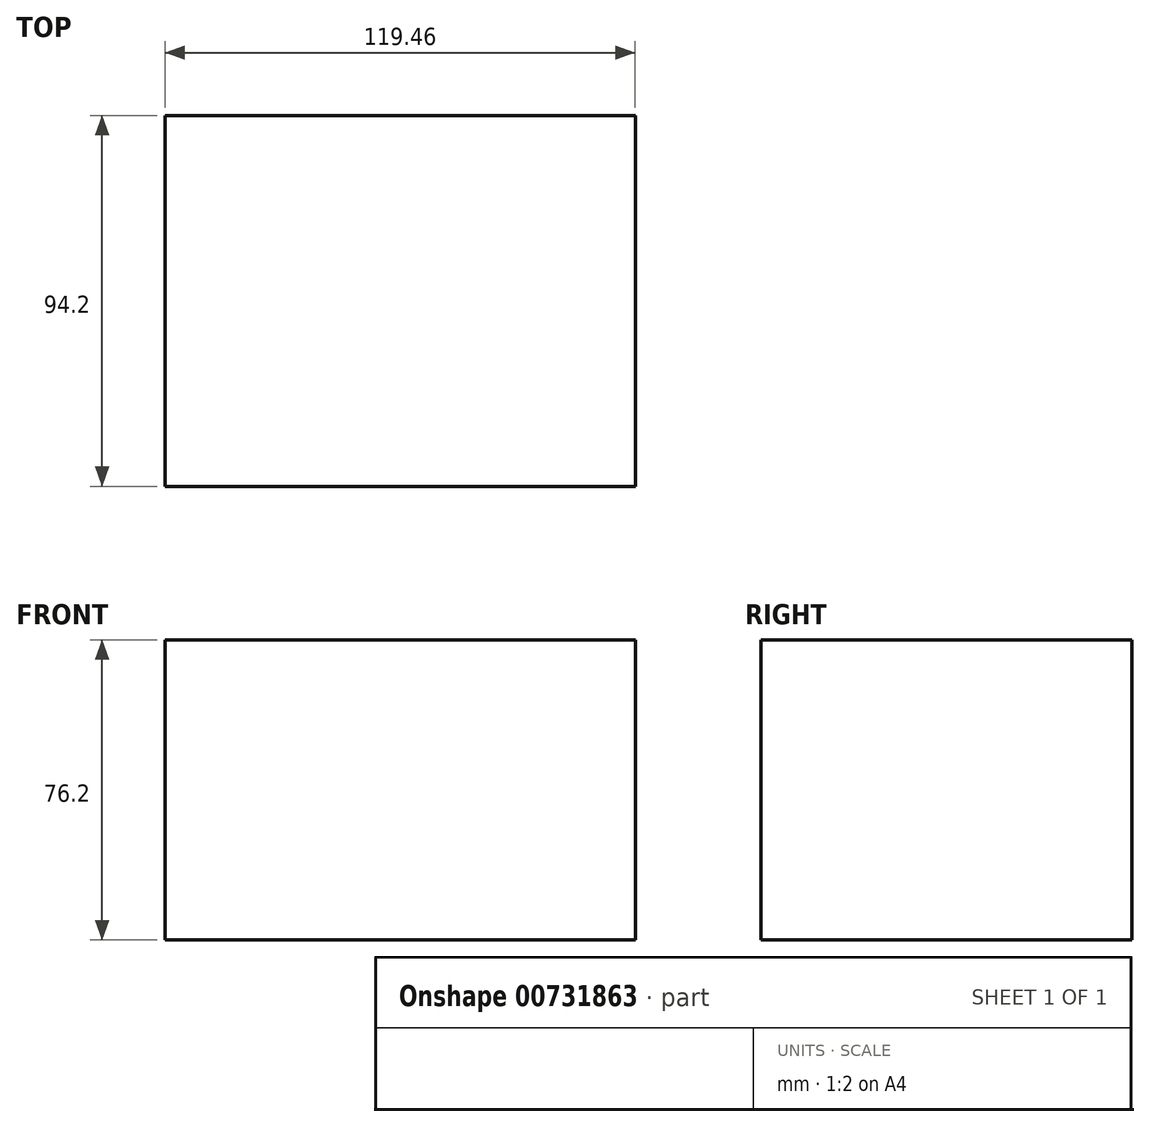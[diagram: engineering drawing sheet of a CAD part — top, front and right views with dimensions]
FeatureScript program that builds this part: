
annotation { "Feature Type Name" : "Feature", "Feature Type Description" : "" }
export const myFeature = defineFeature(function(context is Context, id is Id, definition is map)
    precondition{}
    {
        {
            var Q0;
            Q0=qCreatedBy(makeId("Top.planeOp"),FACE);
            var sketch = newSketch(context, id + "F0", { "sketchPlane" : qUnion([Q0])});
            skLineSegment(sketch, "E0.bottom", {"start": v(-55.4, 45.07) * mm, "end": v(64.06, 45.07) * mm});
            skLineSegment(sketch, "E0.top", {"start": v(-55.4, -49.13) * mm, "end": v(64.06, -49.13) * mm});
            skLineSegment(sketch, "E0.left", {"start": v(-55.4, 45.07) * mm, "end": v(-55.4, -49.13) * mm});
            skLineSegment(sketch, "E0.right", {"start": v(64.06, 45.07) * mm, "end": v(64.06, -49.13) * mm});
            skSolve(sketch);
        }
        {
            var Q0;
            Q0=makeQuery(id+"F0.imprint","IMPRINT",FACE,{"disambiguationData":[TD([[makeQuery(id+"F0.imprint","IMPRINT",EDGE,{"derivedFrom":sQuery(id+"F0.wireOp",EDGE,"E0.bottom")}),-1.0]])]});
            extrude(context, id + "F1", {"entities" : qUnion([Q0]), "depth" : 76.2 * mm, "offsetDistance" : 25.4 * mm});
        }
    });
